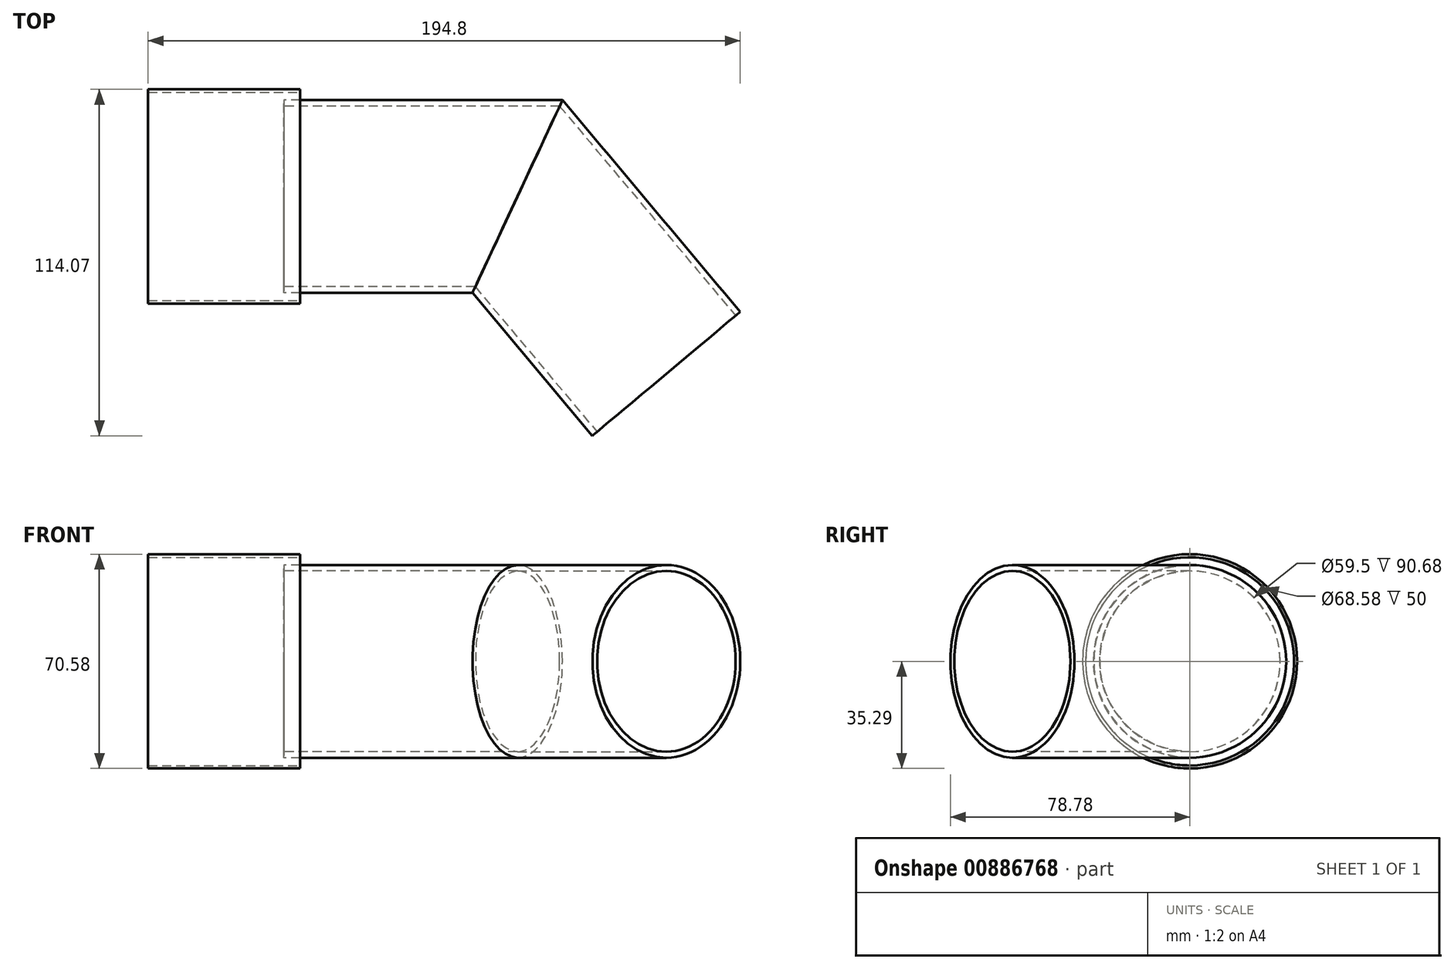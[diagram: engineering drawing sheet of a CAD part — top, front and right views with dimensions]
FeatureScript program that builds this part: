
annotation { "Feature Type Name" : "Feature", "Feature Type Description" : "" }
export const myFeature = defineFeature(function(context is Context, id is Id, definition is map)
    precondition{}
    {
        {
            var Q0;
            Q0=qCreatedBy(makeId("Top.planeOp"),FACE);
            var sketch = newSketch(context, id + "F0", { "sketchPlane" : qUnion([Q0])});
            skLineSegment(sketch, "E0", {"start": v(-76.2, 0) * mm, "end": v(0, 0) * mm});
            skLineSegment(sketch, "E1", {"start": v(0, 0) * mm, "end": v(48.98, -58.37) * mm});
            skSolve(sketch);
        }
        {
            var Q0;
            Q0=qCreatedBy(makeId("Right.planeOp"),FACE);
            cPlane(context, id + "F1", {"entities" : qUnion([Q0]), "cplaneType" : CPlaneType.OFFSET, "offset" : 76.8 * mm, "oppositeDirection" : true, "width" : 150 * mm, "height" : 150 * mm});
        }
        {
            var Q0;
            Q0=qCreatedBy(id+"F1.planeOp",FACE);
            var sketch = newSketch(context, id + "F2", { "sketchPlane" : qUnion([Q0])});
            skCircle(sketch, "E2", {"center": v(0, 0) * mm, "radius": 31.75 * mm});
            skCircle(sketch, "E3.0", {"center": v(0, 0) * mm, "radius": 29.75 * mm});
            skSolve(sketch);
        }
        {
            var Q0;
            Q0=makeQuery(id+"F2.imprint","IMPRINT",FACE,{"disambiguationData":[TD([[makeQuery(id+"F2.imprint","IMPRINT",EDGE,{"derivedFrom":sQuery(id+"F2.wireOp",EDGE,"E2")}),1.0]])]});
            extrude(context, id + "F3", {"entities" : qUnion([Q0]), "depth" : 25 * mm, "offsetDistance" : 25 * mm});
        }
        {
            var Q0;
            Q0=makeQuery(id+"F3.opExtrude","CAP_FACE",FACE,{"disambiguationData":[OSD([sQuery(id+"F2.wireOp",EDGE,"E2"),sQuery(id+"F2.wireOp",EDGE,"E3.0")])],"isStart":false});
            var Q1;
            Q1=sQuery(id+"F0.wireOp",EDGE,"E0");
            var Q2;
            Q2=sQuery(id+"F0.wireOp",EDGE,"E1");
            sweep(context, id + "F4", {"operationType" : NewBodyOperationType.ADD, "profiles" : qUnion([Q0]), "path" : qUnion([Q1, Q2])});
        }
        {
            var Q0;
            Q0=qCreatedBy(id+"F1.planeOp",FACE);
            cPlane(context, id + "F5", {"entities" : qUnion([Q0]), "cplaneType" : CPlaneType.OFFSET, "offset" : 5.3 * mm, "width" : 150 * mm, "height" : 150 * mm});
        }
        {
            var Q0;
            Q0=qCreatedBy(id+"F5.planeOp",FACE);
            var sketch = newSketch(context, id + "F6", { "sketchPlane" : qUnion([Q0])});
            skCircle(sketch, "E4", {"center": v(0, 0) * mm, "radius": 34.3 * mm});
            skCircle(sketch, "E5.0", {"center": v(0, 0) * mm, "radius": 35.29 * mm});
            skSolve(sketch);
        }
        {
            var Q0;
            Q0=makeQuery(id+"F6.imprint","IMPRINT",FACE,{"disambiguationData":[TD([[makeQuery(id+"F6.imprint","IMPRINT",EDGE,{"derivedFrom":sQuery(id+"F6.wireOp",EDGE,"E4")}),-1.0]])]});
            extrude(context, id + "F7", {"entities" : qUnion([Q0]), "oppositeDirection" : true, "depth" : 50 * mm, "offsetDistance" : 25 * mm});
        }
    });
